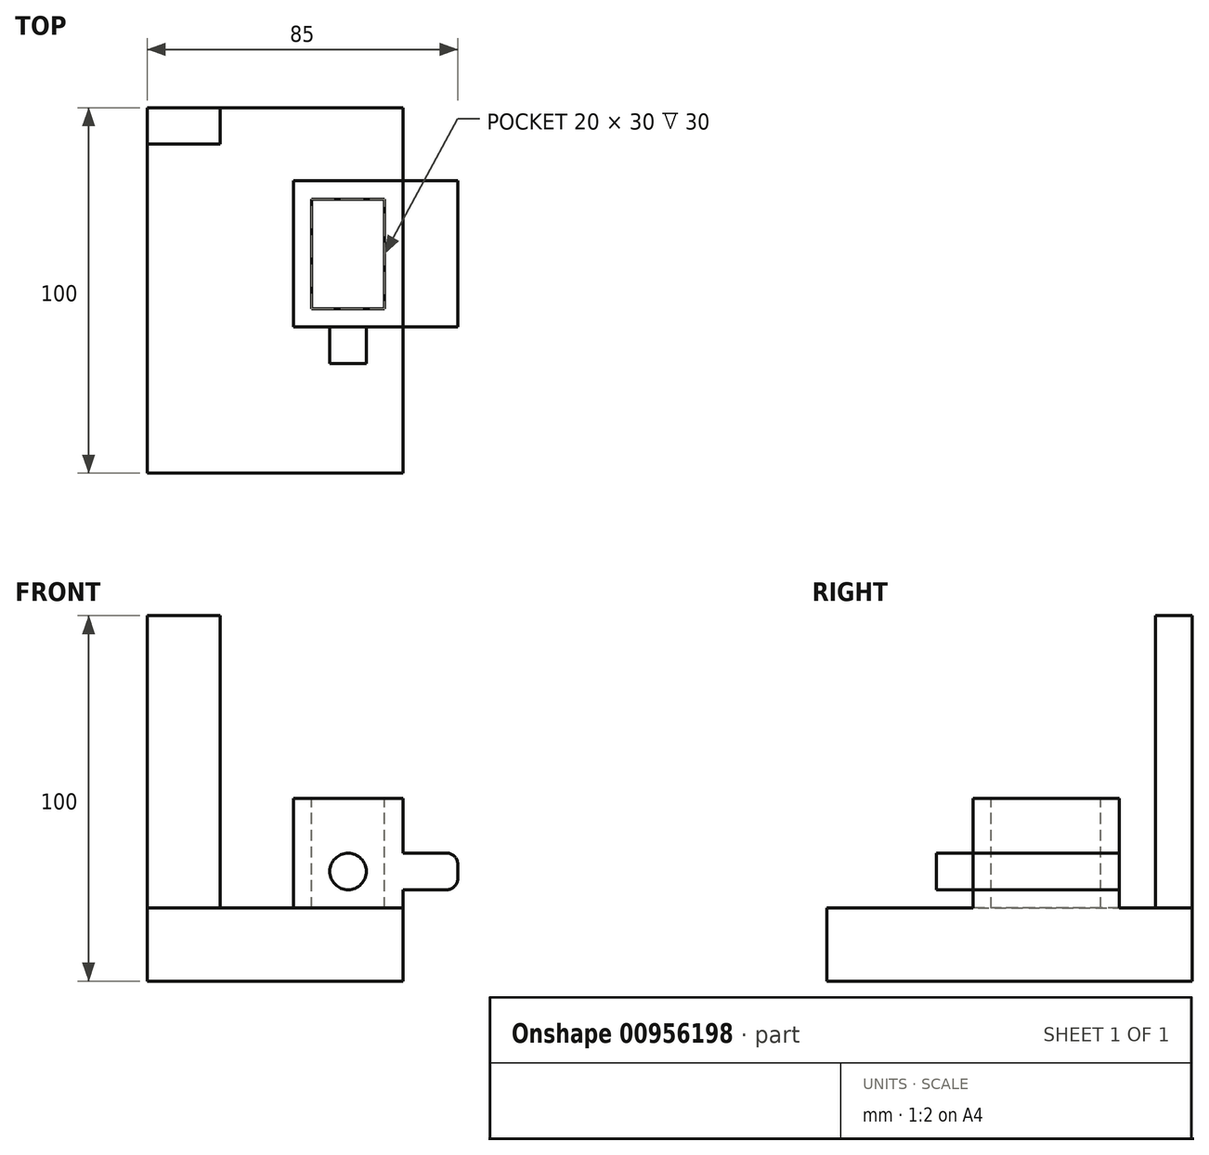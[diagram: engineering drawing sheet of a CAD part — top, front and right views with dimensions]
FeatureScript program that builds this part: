
annotation { "Feature Type Name" : "Feature", "Feature Type Description" : "" }
export const myFeature = defineFeature(function(context is Context, id is Id, definition is map)
    precondition{}
    {
        {
            var Q0;
            Q0=qCreatedBy(makeId("Top.planeOp"),FACE);
            var sketch = newSketch(context, id + "F0", { "sketchPlane" : qUnion([Q0])});
            skLineSegment(sketch, "E0.bottom", {"start": v(0, 0) * mm, "end": v(70, 0) * mm});
            skLineSegment(sketch, "E0.top", {"start": v(0, 100) * mm, "end": v(70, 100) * mm});
            skLineSegment(sketch, "E0.left", {"start": v(0, 0) * mm, "end": v(0, 100) * mm});
            skLineSegment(sketch, "E0.right", {"start": v(70, 0) * mm, "end": v(70, 100) * mm});
            skSolve(sketch);
        }
        {
            var Q0;
            Q0 = qSketchRegion(id + "F0", true);
            extrude(context, id + "F1", {"entities" : qUnion([Q0]), "depth" : 20 * mm, "offsetDistance" : 25 * mm});
        }
        {
            var Q0;
            Q0=makeQuery(id+"F1.opExtrude","CAP_FACE",FACE,{"disambiguationData":[OSD([sQuery(id+"F0.wireOp",EDGE,"E0.bottom"),sQuery(id+"F0.wireOp",EDGE,"E0.top"),sQuery(id+"F0.wireOp",EDGE,"E0.left"),sQuery(id+"F0.wireOp",EDGE,"E0.right")])],"isStart":false});
            var sketch = newSketch(context, id + "F2", { "sketchPlane" : qUnion([Q0])});
            skLineSegment(sketch, "E1.bottom", {"start": v(0, 100) * mm, "end": v(20, 100) * mm});
            skLineSegment(sketch, "E1.top", {"start": v(0, 90) * mm, "end": v(20, 90) * mm});
            skLineSegment(sketch, "E1.left", {"start": v(0, 100) * mm, "end": v(0, 90) * mm});
            skLineSegment(sketch, "E1.right", {"start": v(20, 100) * mm, "end": v(20, 90) * mm});
            skSolve(sketch);
        }
        {
            var Q0;
            Q0 = qSketchRegion(id + "F2", true);
            extrude(context, id + "F3", {"entities" : qUnion([Q0]), "operationType" : NewBodyOperationType.ADD, "depth" : 80 * mm, "offsetDistance" : 25 * mm});
        }
        {
            var Q0;
            Q0=makeQuery(id+"F1.opExtrude","CAP_FACE",FACE,{"disambiguationData":[OSD([sQuery(id+"F0.wireOp",EDGE,"E0.bottom"),sQuery(id+"F0.wireOp",EDGE,"E0.top"),sQuery(id+"F0.wireOp",EDGE,"E0.left"),sQuery(id+"F0.wireOp",EDGE,"E0.right")])],"isStart":false});
            var sketch = newSketch(context, id + "F4", { "sketchPlane" : qUnion([Q0])});
            skLineSegment(sketch, "E2.bottom", {"start": v(70, 80) * mm, "end": v(40, 80) * mm});
            skLineSegment(sketch, "E2.top", {"start": v(70, 40) * mm, "end": v(40, 40) * mm});
            skLineSegment(sketch, "E2.left", {"start": v(70, 80) * mm, "end": v(70, 40) * mm});
            skLineSegment(sketch, "E2.right", {"start": v(40, 80) * mm, "end": v(40, 40) * mm});
            skSolve(sketch);
        }
        {
            var Q0;
            Q0 = qSketchRegion(id + "F4", true);
            extrude(context, id + "F5", {"entities" : qUnion([Q0]), "operationType" : NewBodyOperationType.ADD, "depth" : 30 * mm, "offsetDistance" : 25 * mm});
        }
        {
            var Q0;
            Q0=makeQuery(id+"F5.opExtrude","CAP_FACE",FACE,{"disambiguationData":[OSD([sQuery(id+"F4.wireOp",EDGE,"E2.bottom"),sQuery(id+"F4.wireOp",EDGE,"E2.top"),sQuery(id+"F4.wireOp",EDGE,"E2.left"),sQuery(id+"F4.wireOp",EDGE,"E2.right")])],"isStart":false});
            var sketch = newSketch(context, id + "F6", { "sketchPlane" : qUnion([Q0])});
            skLineSegment(sketch, "E3.0", {"start": v(45, 45) * mm, "end": v(65, 45) * mm});
            skLineSegment(sketch, "E3.1", {"start": v(45, 75) * mm, "end": v(45, 45) * mm});
            skLineSegment(sketch, "E3.2", {"start": v(65, 75) * mm, "end": v(45, 75) * mm});
            skLineSegment(sketch, "E3.3", {"start": v(65, 45) * mm, "end": v(65, 75) * mm});
            skSolve(sketch);
        }
        {
            var Q0;
            Q0=makeQuery(id+"F6.imprint","IMPRINT",FACE,{"disambiguationData":[TD([[makeQuery(id+"F6.imprint","IMPRINT",EDGE,{"derivedFrom":sQuery(id+"F6.wireOp",EDGE,"E3.0")}),1.0]])]});
            extrude(context, id + "F7", {"entities" : qUnion([Q0]), "operationType" : NewBodyOperationType.REMOVE, "oppositeDirection" : true, "depth" : 30 * mm, "offsetDistance" : 25 * mm});
        }
        {
            var Q0;
            Q0=makeQuery(id+"F5.boolean.opBoolean","MERGE",FACE,{"derivedFrom":[makeQuery(id+"F1.opExtrude","SWEPT_FACE",FACE,{"disambiguationData":[OSD([sQuery(id+"F0.wireOp",EDGE,"E0.right")])]}),makeQuery(id+"F5.opExtrude","SWEPT_FACE",FACE,{"disambiguationData":[OSD([sQuery(id+"F4.wireOp",EDGE,"E2.left")])]})]});
            var sketch = newSketch(context, id + "F8", { "sketchPlane" : qUnion([Q0])});
            skLineSegment(sketch, "E4.bottom", {"start": v(80, 35) * mm, "end": v(40, 35) * mm});
            skLineSegment(sketch, "E4.top", {"start": v(80, 25) * mm, "end": v(40, 25) * mm});
            skLineSegment(sketch, "E4.left", {"start": v(80, 35) * mm, "end": v(80, 25) * mm});
            skLineSegment(sketch, "E4.right", {"start": v(40, 35) * mm, "end": v(40, 25) * mm});
            skSolve(sketch);
        }
        {
            var Q0;
            Q0 = qSketchRegion(id + "F8", true);
            extrude(context, id + "F9", {"entities" : qUnion([Q0]), "operationType" : NewBodyOperationType.ADD, "depth" : 15 * mm, "offsetDistance" : 25 * mm});
        }
        {
            var Q0;
            Q0=makeQuery(id+"F9.boolean.opBoolean","MERGE",FACE,{"derivedFrom":[makeQuery(id+"F5.opExtrude","SWEPT_FACE",FACE,{"disambiguationData":[OSD([sQuery(id+"F4.wireOp",EDGE,"E2.top")])]}),makeQuery(id+"F9.opExtrude","SWEPT_FACE",FACE,{"disambiguationData":[OSD([sQuery(id+"F8.wireOp",EDGE,"E4.right")])]})]});
            var sketch = newSketch(context, id + "F10", { "sketchPlane" : qUnion([Q0])});
            skCircle(sketch, "E5", {"center": v(55, 30) * mm, "radius": 5 * mm});
            skSolve(sketch);
        }
        {
            var Q0;
            Q0 = qSketchRegion(id + "F10", true);
            extrude(context, id + "F11", {"entities" : qUnion([Q0]), "operationType" : NewBodyOperationType.ADD, "depth" : 10 * mm, "offsetDistance" : 25 * mm});
        }
        {
            var Q0;
            Q0=makeQuery(id+"F9.opExtrude","CAP_EDGE",EDGE,{"disambiguationData":[OSD([sQuery(id+"F8.wireOp",EDGE,"E4.bottom")])],"isStart":false});
            var Q1;
            Q1=makeQuery(id+"F9.opExtrude","CAP_EDGE",EDGE,{"disambiguationData":[OSD([sQuery(id+"F8.wireOp",EDGE,"E4.top")])],"isStart":false});
            fillet(context, id + "F12", {"entities" : qUnion([Q0, Q1]), "radius" : 3 * mm, "tangentPropagation" : true, "allowEdgeOverflow" : false});
        }
    });
